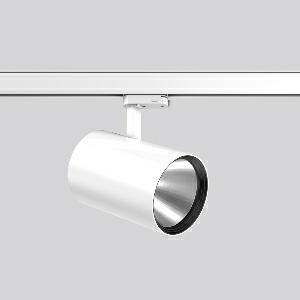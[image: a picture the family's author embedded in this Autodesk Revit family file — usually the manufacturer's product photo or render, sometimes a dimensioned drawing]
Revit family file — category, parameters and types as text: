
# Revit family: deecos_s_maxi_742235_002_99b2
name_source: partatom
category: Lighting Fixtures
units: mm (PartAtom-declared; Revit-internal decimal feet)

## family parameters
Cut with Voids When Loaded = No
Host = Face
Light Source = No
Part Type = Normal
Room Calculation Point = No
Round Connector Dimension = Use Diameter
Shared = No

## types (1)
- DEECOS S maxi (1 x LED Modul 920 meat+, 2250 lm, 2000)
    Apparent Load = 33 VA
    Approval mark = CE
    CIE Flux Codes = 100 100 100 100 100
    Color Rendering = 90
    Color Temperature = 2000
    Default Elevation = 1800 mm
    Description = Series: DEECOS S maxi
LED surface-mounted projector in modern design with no visible cooling ribs. Housing: die-cast aluminium, powder-coated. Rotation range: 356°. Swivel range: 90°. Black plastic ring and recessed LED to prevent glare from the side. Optical assembly with reflector made of MIRO-Silver with 98% total light reflection for outstanding efficiency - can be changed without tools. Special LED for illumination of meat included. With multi adaptor for 3-circuit tracks 230 V. Suitable for Track on ceiling, Wall track. High quality converter without flickering and stroboscopic effect. The following accessories can be mounted without use of tools: interchangeable lenses, decorative glasses, honeycomb louvre, clear and frosted diffusers, white interchangeable plastic ring. 
Colour: traffic white, matt (RAL 9016)
Diameter: 123 mm
Height: 200 mm
Lamp: LED
Socket: without socket
Colour temperature: meat +
System power: 33 W
Rated luminous flux: 2250 lm
Luminous efficiency: 68 lm/W
Control gear: Regulated power supply
Protection class: I
Type of protection: IP 20
    Height = 200 mm  [stored 0.656168 ft]
    Lamp = 1 x LED Modul 920 meat+
    Lamp Light Flux = 2250 lm
    Lamp count = 1
    Length = 123 mm
    Lifetime = 50000 h
    Luminous efficacy = 68 lm/W
    Manufacturer = RZB
    ModVariant = No
    Model = 742235.002
    Mounting Place = Ceiling
    Mounting Type = Rail mounted
    Number of Poles = 1
    OnlyDefault = Yes
    Power Factor = 1
    Product Name = DEECOS S maxi
    Product group = Track mounted projectors
    ProductGroupID = 301
    Protection Class = Protection class I
    Protection Degree = IP 20
    RLX_Detail_Level = 1
    RLX_Emergency_Light_Flux = 0 lm
    RLX_Emergency_Type = 0
    RLX_Emergency_Type_DB = No
    RlxData = <blob elided: 38577 chars, md5=19850349>
    Socket = socket
    Standby Power = 0 W
    System Light Flux = 2250 lm
    System Power = 33 W
    Type Comments = Product without accessories
    Type Image = 741954.002.jpg
    URL = http://relux.com
    VarID = ---
    Voltage = 230 V
    Voltage Range = 220-240 V
    Weight = 0.00 kg
    Width = 0 mm  [stored 0 ft]

note: [stored X ft] marks values corroborated as IEEE doubles in the binary element streams (Revit-internal decimal feet)

## geometry (parser evidence)
native form markers: Blend x4, Sweep x11
no freeform markers — native parametric forms only
